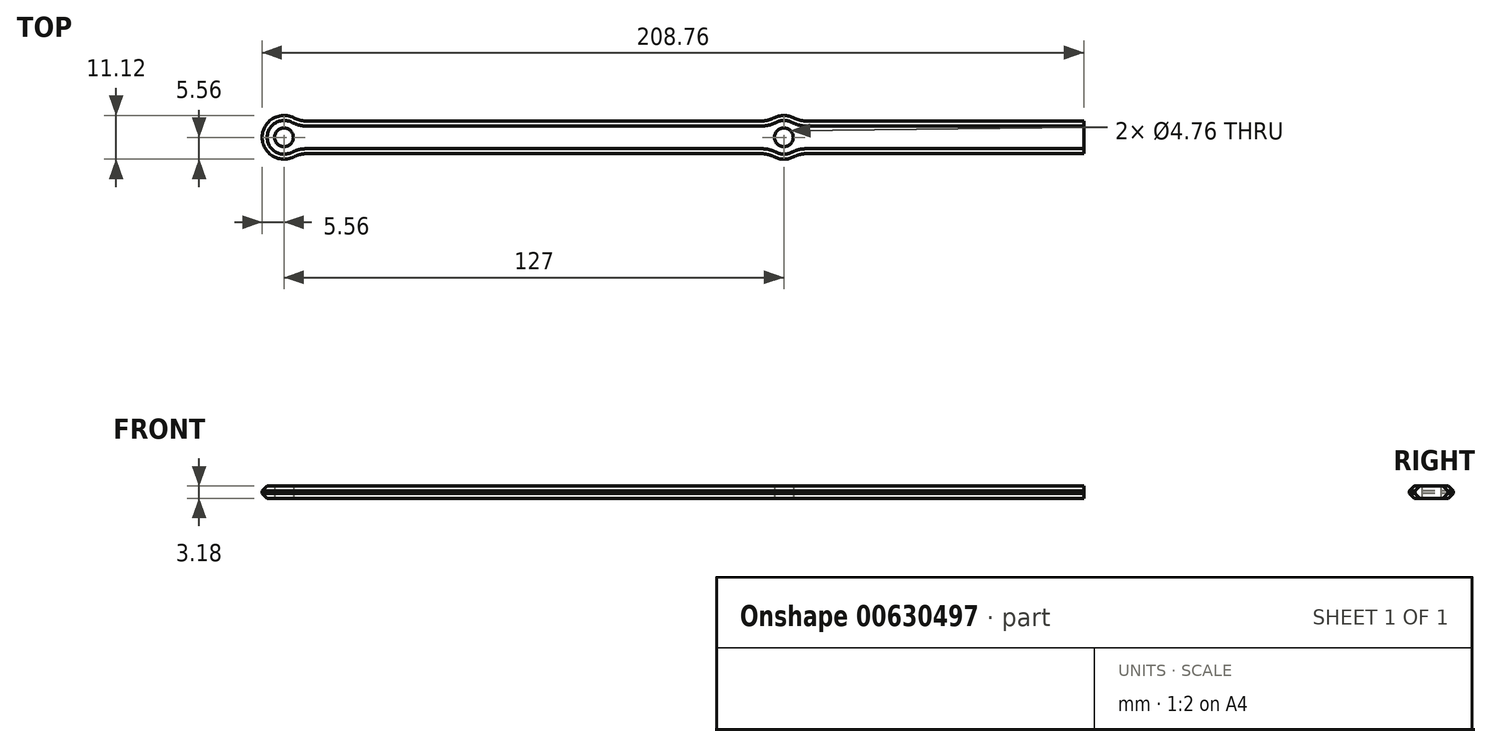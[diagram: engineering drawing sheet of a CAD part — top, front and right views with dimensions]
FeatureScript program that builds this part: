
annotation { "Feature Type Name" : "Feature", "Feature Type Description" : "" }
export const myFeature = defineFeature(function(context is Context, id is Id, definition is map)
    precondition{}
    {
        {
            var Q0;
            Q0=qCreatedBy(makeId("Top.planeOp"),FACE);
            var sketch = newSketch(context, id + "F0", { "sketchPlane" : qUnion([Q0])});
            skCircle(sketch, "E0", {"center": v(0, 0) * mm, "radius": 2.38 * mm});
            skCircle(sketch, "E1", {"center": v(127, 0) * mm, "radius": 2.38 * mm});
            skLineSegment(sketch, "E2", {"start": v(0, 0) * mm, "end": v(127, 0) * mm, "construction": true});
            skArc(sketch, "E3.0", {"start": v(3.68, 4.17) * mm, "mid": v(-5.56, 0) * mm, "end": v(3.68, -4.17) * mm});
            skArc(sketch, "E4.0", {"start": v(123.32, -4.17) * mm, "mid": v(127, -5.56) * mm, "end": v(130.68, -4.17) * mm});
            skLineSegment(sketch, "E5.0.left", {"start": v(3.68, 4.17) * mm, "end": v(123.32, 4.17) * mm});
            skLineSegment(sketch, "E5.0.right", {"start": v(3.68, -4.17) * mm, "end": v(123.32, -4.17) * mm});
            skLineSegment(sketch, "E6", {"start": v(123.32, 4.17) * mm, "end": v(130.68, 4.17) * mm, "construction": true});
            skLineSegment(sketch, "E7", {"start": v(123.32, -4.17) * mm, "end": v(130.68, -4.17) * mm, "construction": true});
            skLineSegment(sketch, "E8", {"start": v(130.68, 4.17) * mm, "end": v(203.2, 4.17) * mm});
            skLineSegment(sketch, "E9", {"start": v(203.2, 4.17) * mm, "end": v(203.2, -4.17) * mm});
            skLineSegment(sketch, "E10", {"start": v(203.2, -4.17) * mm, "end": v(130.68, -4.17) * mm});
            skArc(sketch, "E11.trimOffspring", {"start": v(130.68, 4.17) * mm, "mid": v(127, 5.56) * mm, "end": v(123.32, 4.17) * mm});
            skSolve(sketch);
        }
        {
            var Q0;
            Q0=makeQuery(id+"F0.imprint","IMPRINT",FACE,{"disambiguationData":[TD([[makeQuery(id+"F0.imprint","IMPRINT",EDGE,{"derivedFrom":sQuery(id+"F0.wireOp",EDGE,"E0")}),-1.0]])]});
            extrude(context, id + "F1", {"entities" : qUnion([Q0]), "depth" : 3.17 * mm, "offsetDistance" : 25.4 * mm});
        }
        {
            var Q0;
            Q0=makeQuery(id+"F1.opExtrude","SWEPT_EDGE",EDGE,{"disambiguationData":[OSD([sQuery(id+"F0.wireOp",EDGE,"E3.0"),sQuery(id+"F0.wireOp",EDGE,"E5.0.left")])]});
            var Q1;
            Q1=makeQuery(id+"F1.opExtrude","SWEPT_EDGE",EDGE,{"disambiguationData":[OSD([sQuery(id+"F0.wireOp",EDGE,"E3.0"),sQuery(id+"F0.wireOp",EDGE,"E5.0.right")])]});
            var Q2;
            Q2=makeQuery(id+"F1.opExtrude","SWEPT_EDGE",EDGE,{"disambiguationData":[OSD([sQuery(id+"F0.wireOp",EDGE,"E4.0"),sQuery(id+"F0.wireOp",EDGE,"E5.0.right")])]});
            var Q3;
            Q3=makeQuery(id+"F1.opExtrude","SWEPT_EDGE",EDGE,{"disambiguationData":[OSD([sQuery(id+"F0.wireOp",EDGE,"E4.0"),sQuery(id+"F0.wireOp",EDGE,"E5.0.left")])]});
            var Q4;
            Q4=makeQuery(id+"F1.opExtrude","SWEPT_EDGE",EDGE,{"disambiguationData":[OSD([sQuery(id+"F0.wireOp",EDGE,"E8"),sQuery(id+"F0.wireOp",EDGE,"E11.trimOffspring")])]});
            fillet(context, id + "F2", {"entities" : qUnion([Q0, Q1, Q2, Q3, Q4]), "radius" : 6.35 * mm, "tangentPropagation" : true, "allowEdgeOverflow" : false});
        }
        {
            var Q0;
            Q0=makeQuery(id+"F1.opExtrude","CAP_EDGE",EDGE,{"disambiguationData":[OSD([sQuery(id+"F0.wireOp",EDGE,"E5.0.left")])],"isStart":false});
            var Q1;
            Q1=makeQuery(id+"F1.opExtrude","CAP_EDGE",EDGE,{"disambiguationData":[OSD([sQuery(id+"F0.wireOp",EDGE,"E5.0.left")])],"isStart":true});
            chamfer(context, id + "F3", {"entities" : qUnion([Q0, Q1]), "width" : 1.27 * mm, "tangentPropagation" : true});
        }
    });
